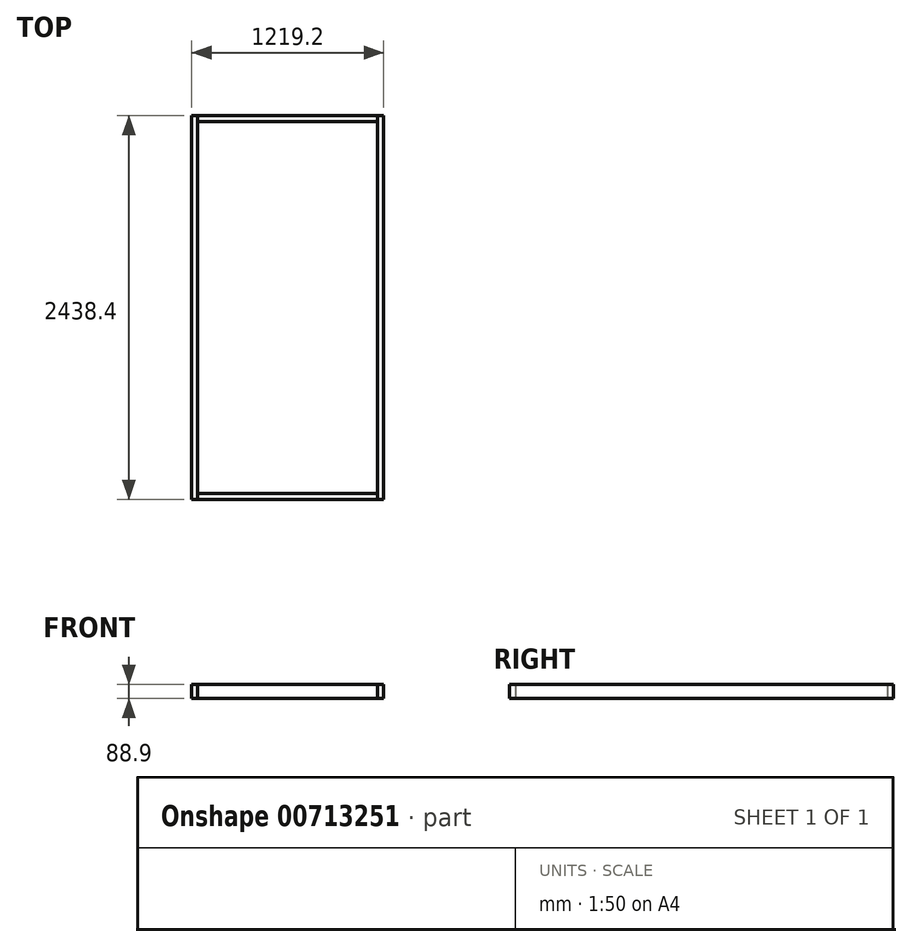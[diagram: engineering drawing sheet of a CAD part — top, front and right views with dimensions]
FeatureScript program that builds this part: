
annotation { "Feature Type Name" : "Feature", "Feature Type Description" : "" }
export const myFeature = defineFeature(function(context is Context, id is Id, definition is map)
    precondition{}
    {
        {
            var Q0;
            Q0=qCreatedBy(makeId("Front.planeOp"),FACE);
            var sketch = newSketch(context, id + "F0", { "sketchPlane" : qUnion([Q0])});
            skLineSegment(sketch, "E0", {"start": v(-590.55, 0) * mm, "end": v(590.55, 0) * mm, "construction": true});
            skPoint(sketch, "E1", {"position": v(0, 0) * mm});
            skLineSegment(sketch, "E2.bottom", {"start": v(-571.5, -44.45) * mm, "end": v(-609.6, -44.45) * mm});
            skLineSegment(sketch, "E2.top", {"start": v(-571.5, 44.45) * mm, "end": v(-609.6, 44.45) * mm});
            skLineSegment(sketch, "E2.left", {"start": v(-571.5, -44.45) * mm, "end": v(-571.5, 44.45) * mm});
            skLineSegment(sketch, "E2.right", {"start": v(-609.6, -44.45) * mm, "end": v(-609.6, 44.45) * mm});
            skPoint(sketch, "E2.middle", {"position": v(-590.55, 0) * mm});
            skLineSegment(sketch, "E3.bottom", {"start": v(571.5, -44.45) * mm, "end": v(609.6, -44.45) * mm});
            skLineSegment(sketch, "E3.top", {"start": v(571.5, 44.45) * mm, "end": v(609.6, 44.45) * mm});
            skLineSegment(sketch, "E3.left", {"start": v(571.5, -44.45) * mm, "end": v(571.5, 44.45) * mm});
            skLineSegment(sketch, "E3.right", {"start": v(609.6, -44.45) * mm, "end": v(609.6, 44.45) * mm});
            skPoint(sketch, "E3.middle", {"position": v(590.55, 0) * mm});
            skSolve(sketch);
        }
        {
            var Q0;
            Q0 = qSketchRegion(id + "F0", true);
            extrude(context, id + "F1", {"entities" : qUnion([Q0]), "endBound" : BoundingType.SYMMETRIC, "depth" : 2438.4 * mm, "offsetDistance" : 25.4 * mm});
        }
        {
            var Q0;
            Q0=makeQuery(id+"F1.opExtrude","SWEPT_FACE",FACE,{"disambiguationData":[OSD([sQuery(id+"F0.wireOp",EDGE,"E2.left")])]});
            var sketch = newSketch(context, id + "F2", { "sketchPlane" : qUnion([Q0])});
            skLineSegment(sketch, "E4.bottom", {"start": v(-1219.2, 44.45) * mm, "end": v(-1181.1, 44.45) * mm});
            skLineSegment(sketch, "E4.top", {"start": v(-1219.2, -44.45) * mm, "end": v(-1181.1, -44.45) * mm});
            skLineSegment(sketch, "E4.left", {"start": v(-1219.2, 44.45) * mm, "end": v(-1219.2, -44.45) * mm});
            skLineSegment(sketch, "E4.right", {"start": v(-1181.1, 44.45) * mm, "end": v(-1181.1, -44.45) * mm});
            skLineSegment(sketch, "E5.bottom", {"start": v(1219.2, 44.45) * mm, "end": v(1181.1, 44.45) * mm});
            skLineSegment(sketch, "E5.top", {"start": v(1219.2, -44.45) * mm, "end": v(1181.1, -44.45) * mm});
            skLineSegment(sketch, "E5.left", {"start": v(1219.2, 44.45) * mm, "end": v(1219.2, -44.45) * mm});
            skLineSegment(sketch, "E5.right", {"start": v(1181.1, 44.45) * mm, "end": v(1181.1, -44.45) * mm});
            skSolve(sketch);
        }
        {
            var Q0;
            Q0 = qSketchRegion(id + "F2", true);
            extrude(context, id + "F3", {"entities" : qUnion([Q0]), "depth" : 1143 * mm, "offsetDistance" : 25.4 * mm});
        }
    });
